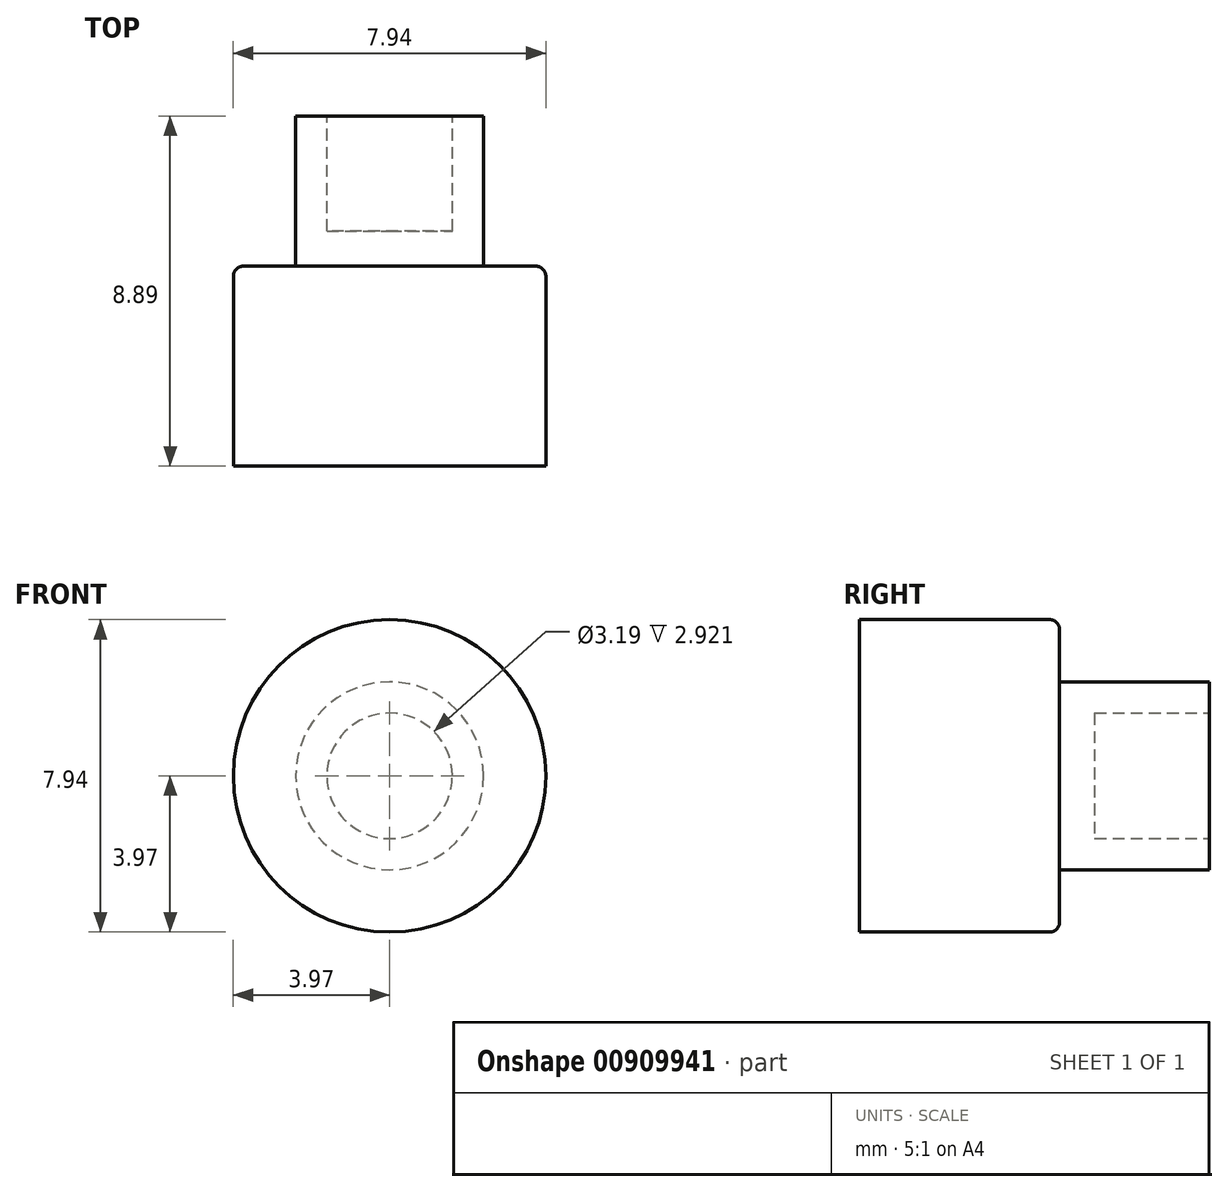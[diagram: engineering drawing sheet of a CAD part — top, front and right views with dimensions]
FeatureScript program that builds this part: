
annotation { "Feature Type Name" : "Feature", "Feature Type Description" : "" }
export const myFeature = defineFeature(function(context is Context, id is Id, definition is map)
    precondition{}
    {
        {
            var Q0;
            Q0=qCreatedBy(makeId("Front.planeOp"),FACE);
            var sketch = newSketch(context, id + "F0", { "sketchPlane" : qUnion([Q0])});
            skCircle(sketch, "E0", {"center": v(0, 0) * mm, "radius": 2.39 * mm});
            skSolve(sketch);
        }
        {
            var Q0;
            Q0 = qSketchRegion(id + "F0", true);
            extrude(context, id + "F1", {"entities" : qUnion([Q0]), "depth" : 3.8 * mm, "offsetDistance" : 25.4 * mm});
        }
        {
            var Q0;
            Q0=makeQuery(id+"F1.opExtrude","CAP_FACE",FACE,{"disambiguationData":[OSD([sQuery(id+"F0.wireOp",EDGE,"E0")])],"isStart":false});
            var sketch = newSketch(context, id + "F2", { "sketchPlane" : qUnion([Q0])});
            skCircle(sketch, "E1", {"center": v(0, 0) * mm, "radius": 3.97 * mm});
            skSolve(sketch);
        }
        {
            var Q0;
            Q0 = qSketchRegion(id + "F2", true);
            extrude(context, id + "F3", {"entities" : qUnion([Q0]), "operationType" : NewBodyOperationType.ADD, "depth" : 5.08 * mm, "offsetDistance" : 25.4 * mm});
        }
        {
            var Q0;
            Q0=makeQuery(id+"F1.opExtrude","CAP_FACE",FACE,{"disambiguationData":[OSD([sQuery(id+"F0.wireOp",EDGE,"E0")])],"isStart":true});
            var sketch = newSketch(context, id + "F4", { "sketchPlane" : qUnion([Q0])});
            skCircle(sketch, "E2", {"center": v(0, 0) * mm, "radius": 1.6 * mm});
            skSolve(sketch);
        }
        {
            var Q0;
            Q0=makeQuery(id+"F4.imprint","IMPRINT",FACE,{"disambiguationData":[TD([[makeQuery(id+"F4.imprint","IMPRINT",EDGE,{"derivedFrom":sQuery(id+"F4.wireOp",EDGE,"E2")}),1.0]])]});
            extrude(context, id + "F5", {"entities" : qUnion([Q0]), "operationType" : NewBodyOperationType.REMOVE, "oppositeDirection" : true, "depth" : 2.92 * mm, "offsetDistance" : 25.4 * mm});
        }
        {
            var Q0;
            Q0=makeQuery(id+"F3.opExtrude","CAP_EDGE",EDGE,{"disambiguationData":[OSD([sQuery(id+"F2.wireOp",EDGE,"E1")])],"isStart":true});
            fillet(context, id + "F6", {"entities" : qUnion([Q0]), "radius" : 0.25 * mm, "tangentPropagation" : true, "allowEdgeOverflow" : false});
        }
    });
